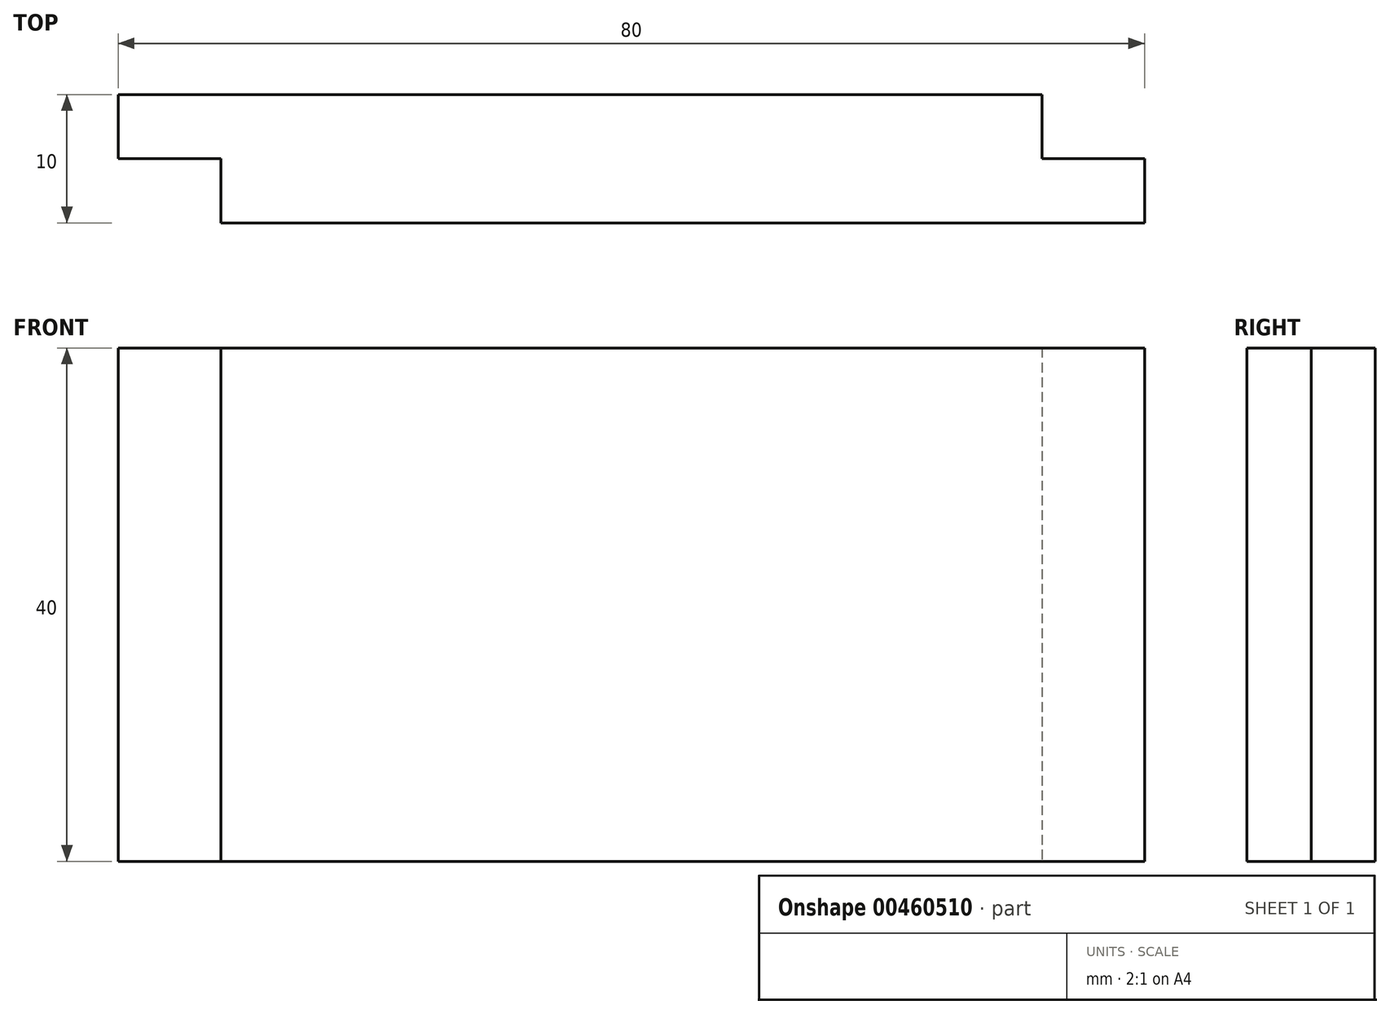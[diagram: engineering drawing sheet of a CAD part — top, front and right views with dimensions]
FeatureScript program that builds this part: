
annotation { "Feature Type Name" : "Feature", "Feature Type Description" : "" }
export const myFeature = defineFeature(function(context is Context, id is Id, definition is map)
    precondition{}
    {
        {
            var Q0;
            Q0=qCreatedBy(makeId("Top.planeOp"),FACE);
            var sketch = newSketch(context, id + "F0", { "sketchPlane" : qUnion([Q0])});
            skLineSegment(sketch, "E0.bottom", {"start": v(8, 0) * mm, "end": v(80, 0) * mm});
            skLineSegment(sketch, "E0.top", {"start": v(0, 10) * mm, "end": v(72, 10) * mm});
            skLineSegment(sketch, "E0.left", {"start": v(0, 5) * mm, "end": v(0, 10) * mm});
            skLineSegment(sketch, "E0.right", {"start": v(80, 0) * mm, "end": v(80, 5) * mm});
            skLineSegment(sketch, "E1", {"start": v(0, 5) * mm, "end": v(8, 5) * mm});
            skPoint(sketch, "E1.endSnap0", {"position": v(0, 5) * mm});
            skLineSegment(sketch, "E2", {"start": v(8, 5) * mm, "end": v(8, 0) * mm});
            skLineSegment(sketch, "E3", {"start": v(80, 5) * mm, "end": v(72, 5) * mm});
            skLineSegment(sketch, "E4", {"start": v(72, 5) * mm, "end": v(72, 10) * mm});
            skPoint(sketch, "E5.orphan", {"position": v(80, 10) * mm});
            skPoint(sketch, "E6.orphan", {"position": v(0, 0) * mm});
            skSolve(sketch);
        }
        {
            var Q0;
            Q0 = qSketchRegion(id + "F0", true);
            extrude(context, id + "F1", {"entities" : qUnion([Q0]), "depth" : 40 * mm});
        }
    });
